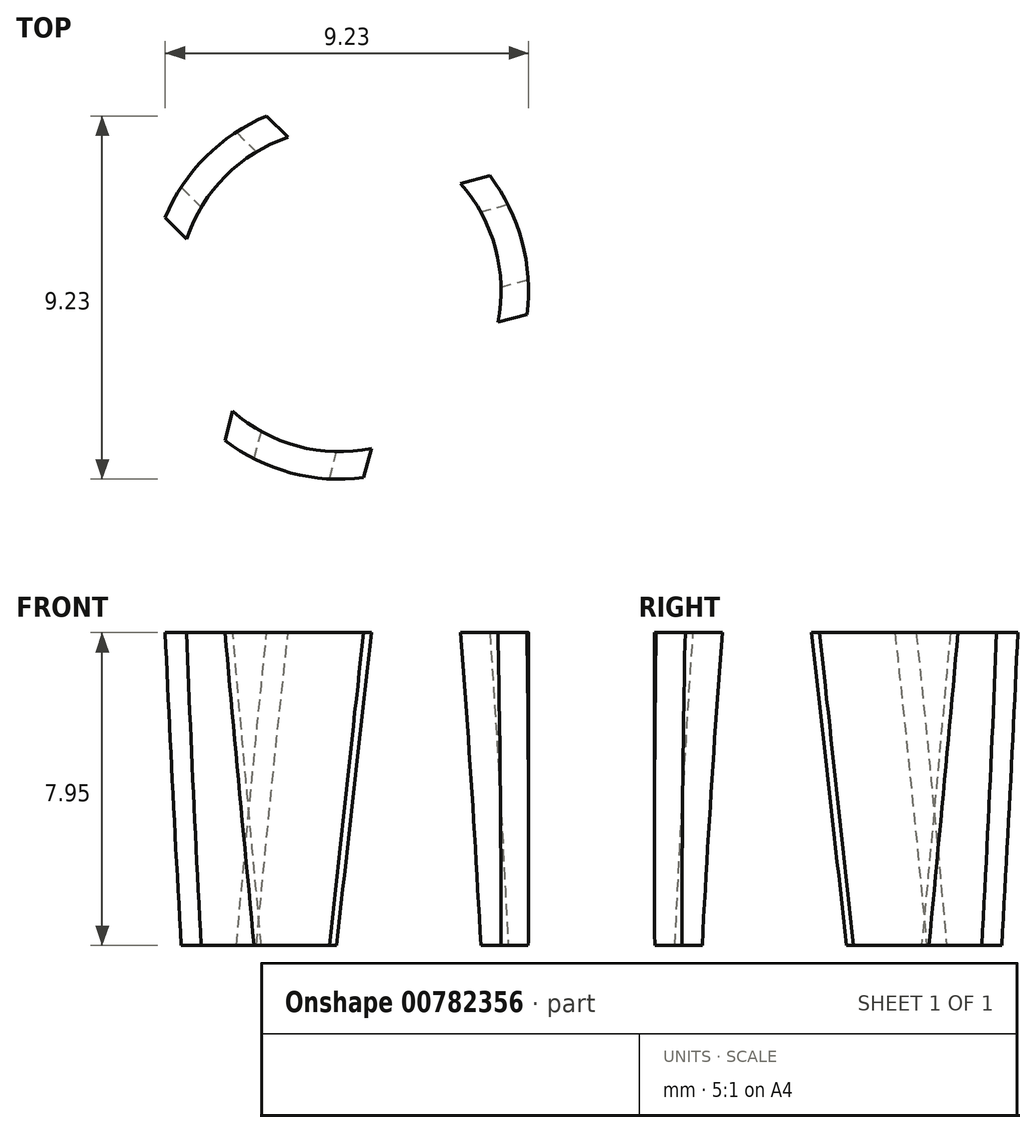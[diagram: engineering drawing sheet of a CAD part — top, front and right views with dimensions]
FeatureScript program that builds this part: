
annotation { "Feature Type Name" : "Feature", "Feature Type Description" : "" }
export const myFeature = defineFeature(function(context is Context, id is Id, definition is map)
    precondition{}
    {
        {
            var Q0;
            Q0=qCreatedBy(makeId("Front.planeOp"),FACE);
            var sketch = newSketch(context, id + "F0", { "sketchPlane" : qUnion([Q0])});
            skLineSegment(sketch, "E0", {"start": v(0, 0) * mm, "end": v(0, 13.85) * mm});
            skSolve(sketch);
        }
        {
            var Q0;
            Q0=sQuery(id+"F0.wireOp",EDGE,"E0");
            cPlane(context, id + "F1", {"entities" : qUnion([Q0]), "cplaneType" : CPlaneType.LINE_ANGLE, "offset" : 25 * mm, "angle" : 15 * degree, "width" : 150 * mm, "height" : 150 * mm});
        }
        {
            var Q0;
            Q0=qCreatedBy(id+"F1.planeOp",FACE);
            var sketch = newSketch(context, id + "F2", { "sketchPlane" : qUnion([Q0])});
            skLineSegment(sketch, "E1.bottom", {"start": v(7, -1) * mm, "end": v(-7, -1) * mm});
            skLineSegment(sketch, "E1.top", {"start": v(7, 1) * mm, "end": v(-7, 1) * mm});
            skLineSegment(sketch, "E1.left", {"start": v(7, -1) * mm, "end": v(7, 1) * mm});
            skLineSegment(sketch, "E1.right", {"start": v(-7, -1) * mm, "end": v(-7, 1) * mm});
            skPoint(sketch, "E1.middle", {"position": v(0, 0) * mm});
            skLineSegment(sketch, "E2", {"start": v(0, 1) * mm, "end": v(0, -1) * mm});
            skLineSegment(sketch, "E3.bottom", {"start": v(0, -1) * mm, "end": v(4.8, -1) * mm});
            skLineSegment(sketch, "E3.top", {"start": v(0, 8.95) * mm, "end": v(4.8, 8.95) * mm});
            skLineSegment(sketch, "E3.left", {"start": v(0, -1) * mm, "end": v(0, 8.95) * mm});
            skLineSegment(sketch, "E3.right", {"start": v(4.8, -1) * mm, "end": v(4.8, 8.95) * mm});
            skLineSegment(sketch, "E4", {"start": v(4.1, 8.95) * mm, "end": v(4.1, -1) * mm});
            skLineSegment(sketch, "E5", {"start": v(1.46, 5.5) * mm, "end": v(1.82, 8.95) * mm});
            skLineSegment(sketch, "E6", {"start": v(-1.46, 5.5) * mm, "end": v(-1.83, 8.95) * mm});
            skLineSegment(sketch, "E7", {"start": v(-1.83, 8.95) * mm, "end": v(0, 8.95) * mm});
            skPoint(sketch, "E8", {"position": v(-1.46, 5.5) * mm});
            skPoint(sketch, "E9", {"position": v(1.46, 5.5) * mm});
            skLineSegment(sketch, "E10", {"start": v(-1.46, 5.5) * mm, "end": v(-1.46, 1) * mm});
            skLineSegment(sketch, "E11", {"start": v(1.46, 5.5) * mm, "end": v(1.46, 1) * mm});
            skLineSegment(sketch, "E12", {"start": v(-1.46, 5.5) * mm, "end": v(-0.99, 1) * mm});
            skLineSegment(sketch, "E13", {"start": v(1.46, 5.5) * mm, "end": v(0.99, 1) * mm});
            skSolve(sketch);
        }
        {
            var Q0;
            {var subQ0=sQuery(id+"F2.wireOp",EDGE,"E1.left");Q0=makeQuery(id+"F2.imprint","IMPRINT",FACE,{"disambiguationData":[TD([[makeQuery(id+"F2.imprint","IMPRINT",EDGE,{"derivedFrom":subQ0}),1.0]])]});}
            var Q1;
            {var subQ7=sQuery(id+"F2.wireOp",EDGE,"vqbd3tU6-uZOk-y5DT-lw4q-ojvEtcCSjOwh");Q1=makeQuery(id+"F2.imprint","IMPRINT",FACE,{"disambiguationData":[TD([[makeQuery(id+"F2.imprint","IMPRINT",EDGE,{"derivedFrom":subQ7}),-1.0]])]});}
            var Q2;
            {var subQ0=sQuery(id+"F2.wireOp",EDGE,"E1.right");Q2=makeQuery(id+"F2.imprint","IMPRINT",FACE,{"disambiguationData":[TD([[makeQuery(id+"F2.imprint","IMPRINT",EDGE,{"derivedFrom":subQ0}),-1.0]])]});}
            var Q3;
            {var subQ0=sQuery(id+"F2.wireOp",EDGE,"E3.right");var subQ1=sQuery(id+"F2.wireOp",EDGE,"E1.top");var subQ2=makeQuery(id+"F2.imprint","INTERSECT",VERTEX,{"derivedFrom":[subQ1,subQ0]});Q3=makeQuery(id+"F2.imprint","IMPRINT",FACE,{"disambiguationData":[TD([[makeQuery(id+"F2.imprint","IMPRINT",EDGE,{"disambiguationData":[TD([[subQ2,-1.0]])],"derivedFrom":subQ1}),1.0]])]});}
            var Q4;
            Q4=sQuery(id+"F2.wireOp",EDGE,"E2");
            revolve(context, id + "F3", {"surfaceOperationType" : NewSurfaceOperationType.NEW, "entities" : qUnion([Q0, Q1, Q2, Q3]), "axis" : qUnion([Q4]), "revolveType" : RevolveType.FULL});
        }
        {
            var Q0;
            {var subQ0=sQuery(id+"F2.wireOp",EDGE,"E3.right");var subQ1=sQuery(id+"F2.wireOp",EDGE,"E1.top");var subQ2=makeQuery(id+"F2.imprint","INTERSECT",VERTEX,{"derivedFrom":[subQ1,subQ0]});Q0=makeQuery(id+"F2.imprint","IMPRINT",FACE,{"disambiguationData":[TD([[makeQuery(id+"F2.imprint","IMPRINT",EDGE,{"disambiguationData":[TD([[subQ2,-1.0]])],"derivedFrom":subQ1}),-1.0]])]});}
            var Q1;
            {var subQ0=sQuery(id+"F2.wireOp",EDGE,"E3.right");var subQ1=sQuery(id+"F2.wireOp",EDGE,"E1.top");var subQ2=makeQuery(id+"F2.imprint","INTERSECT",VERTEX,{"derivedFrom":[subQ1,subQ0]});Q1=makeQuery(id+"F2.imprint","IMPRINT",FACE,{"disambiguationData":[TD([[makeQuery(id+"F2.imprint","IMPRINT",EDGE,{"disambiguationData":[TD([[subQ2,-1.0]])],"derivedFrom":subQ1}),1.0]])]});}
            var Q2;
            Q2=sQuery(id+"F2.wireOp",EDGE,"E3.left");
            revolve(context, id + "F4", {"surfaceOperationType" : NewSurfaceOperationType.NEW, "entities" : qUnion([Q0, Q1]), "axis" : qUnion([Q2]), "revolveType" : RevolveType.FULL});
        }
        {
            var Q0;
            {var subQ0=sQuery(id+"F2.wireOp",EDGE,"E5");Q0=makeQuery(id+"F2.imprint","IMPRINT",FACE,{"disambiguationData":[TD([[makeQuery(id+"F2.imprint","IMPRINT",EDGE,{"derivedFrom":subQ0}),1.0]])]});}
            var Q1;
            Q1=makeQuery(id+"F2.imprint","IMPRINT",FACE,{"disambiguationData":[TD([[makeQuery(id+"F2.imprint","IMPRINT",EDGE,{"derivedFrom":sQuery(id+"F2.wireOp",EDGE,"E6")}),-1.0]])]});
            extrude(context, id + "F5", {"entities" : qUnion([Q0, Q1]), "depth" : 5.6 * mm, "offsetDistance" : 25 * mm});
        }
        {
            var Q0;
            Q0=makeQuery(id+"F5.opExtrude","SWEPT_BODY",BODY,{"disambiguationData":[OSD([sQuery(id+"F2.wireOp",EDGE,"E3.top"),sQuery(id+"F2.wireOp",EDGE,"vqbd3tU6-uZOk-y5DT-lw4q-ojvEtcCSjOwh"),sQuery(id+"F2.wireOp",EDGE,"E5"),sQuery(id+"F2.wireOp",EDGE,"KzomdtZ3-JvvX-BvCP-MlnV-1LGT3AlAoch6"),sQuery(id+"F2.wireOp",EDGE,"E6"),sQuery(id+"F2.wireOp",EDGE,"E7")])]});
            var Q1;
            Q1=sQuery(id+"F2.wireOp",EDGE,"E3.left");
            circularPattern(context, id + "F6", {"operationType" : NewBodyOperationType.INTERSECT, "entities" : qUnion([Q0]), "axis" : qUnion([Q1]), "angle" : 360 * degree, "instanceCount" : 3, "equalSpace" : true});
        }
    });
